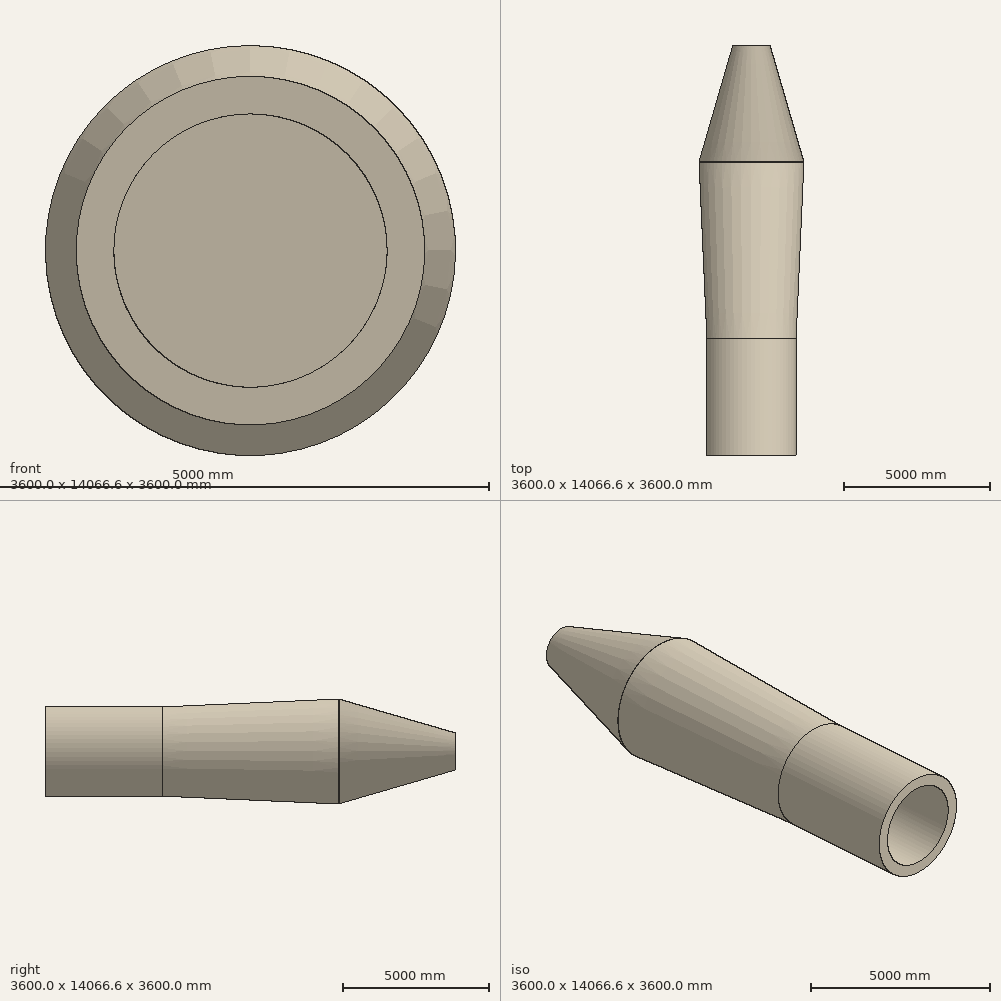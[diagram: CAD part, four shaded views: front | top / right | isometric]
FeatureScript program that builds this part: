
annotation { "Feature Type Name" : "Feature", "Feature Type Description" : "" }
export const myFeature = defineFeature(function(context is Context, id is Id, definition is map)
    precondition{}
    {
        {
            var Q0;
            Q0=qCreatedBy(makeId("Right.planeOp"),FACE);
            var sketch = newSketch(context, id + "F0", { "sketchPlane" : qUnion([Q0])});
            skLineSegment(sketch, "E0", {"start": v(0, 0) * mm, "end": v(-3999.63, 0) * mm});
            skLineSegment(sketch, "E1", {"start": v(-3999.63, 1800) * mm, "end": v(0, 637.5) * mm});
            skLineSegment(sketch, "E2", {"start": v(0, 0) * mm, "end": v(0, 637.5) * mm});
            skLineSegment(sketch, "E3", {"start": v(-3999.63, 0) * mm, "end": v(-10066.63, 0) * mm});
            skLineSegment(sketch, "E4", {"start": v(-10066.63, 1530) * mm, "end": v(-3999.63, 1800) * mm});
            skLineSegment(sketch, "E5", {"start": v(-10066.63, 0) * mm, "end": v(-14066.63, 0) * mm});
            skLineSegment(sketch, "E6", {"start": v(-14066.63, 0) * mm, "end": v(-14066.63, 1530) * mm});
            skLineSegment(sketch, "E7", {"start": v(-14066.63, 1530) * mm, "end": v(-10066.63, 1530) * mm});
            skSolve(sketch);
        }
        {
            var Q0;
            Q0=makeQuery(id+"F0.imprint","IMPRINT",FACE,{"disambiguationData":[TD([[makeQuery(id+"F0.imprint","IMPRINT",EDGE,{"derivedFrom":sQuery(id+"F0.wireOp",EDGE,"E0")}),-1.0]])]});
            var sketch = newSketch(context, id + "F1", { "sketchPlane" : qUnion([Q0])});
            skLineSegment(sketch, "E8", {"start": v(-10067, 0) * mm, "end": v(-2000, 0) * mm});
            skLineSegment(sketch, "E9", {"start": v(-2000, 0) * mm, "end": v(-2000, 1200) * mm});
            skLineSegment(sketch, "E10", {"start": v(-2000, 1200) * mm, "end": v(-10067, 1200) * mm});
            skLineSegment(sketch, "E11", {"start": v(0, 0) * mm, "end": v(0, 1369) * mm, "construction": true});
            skLineSegment(sketch, "E12", {"start": v(0, 1369) * mm, "end": v(-10067, 4000) * mm, "construction": true});
            skLineSegment(sketch, "E13", {"start": v(-10067, 0) * mm, "end": v(0, 0) * mm, "construction": true});
            skLineSegment(sketch, "E14", {"start": v(-10067, 0) * mm, "end": v(-14067.43, 0) * mm});
            skLineSegment(sketch, "E15", {"start": v(-14067.43, 0) * mm, "end": v(-14067.43, 1200) * mm});
            skLineSegment(sketch, "E16", {"start": v(-14067.43, 1200) * mm, "end": v(-10067, 1200) * mm});
            skSolve(sketch);
        }
        {
            var Q0;
            Q0=qCreatedBy(makeId("Right.planeOp"),FACE);
            var sketch = newSketch(context, id + "F2", { "sketchPlane" : qUnion([Q0])});
            skLineSegment(sketch, "E17.bottom", {"start": v(0, 0) * mm, "end": v(-1524, 0) * mm});
            skLineSegment(sketch, "E17.top", {"start": v(0, 630) * mm, "end": v(-1524, 630) * mm});
            skLineSegment(sketch, "E17.left", {"start": v(0, 0) * mm, "end": v(0, 630) * mm});
            skLineSegment(sketch, "E17.right", {"start": v(-1524, 0) * mm, "end": v(-1524, 630) * mm});
            skSolve(sketch);
        }
        {
            var Q0;
            Q0=makeQuery(id+"F0.imprint","IMPRINT",FACE,{"disambiguationData":[TD([[makeQuery(id+"F0.imprint","IMPRINT",EDGE,{"derivedFrom":sQuery(id+"F0.wireOp",EDGE,"E0")}),-1.0]])]});
            var sketch = newSketch(context, id + "F3", { "sketchPlane" : qUnion([Q0])});
            skLineSegment(sketch, "E18", {"start": v(-10067, 0) * mm, "end": v(-10067, 1500) * mm});
            skLineSegment(sketch, "E19", {"start": v(-10067, 1500) * mm, "end": v(-3985, 1798.69) * mm});
            skLineSegment(sketch, "E20", {"start": v(-3985, 1798.69) * mm, "end": v(-3985, 0) * mm});
            skLineSegment(sketch, "E21", {"start": v(-3985, 0) * mm, "end": v(-10067, 0) * mm});
            skSolve(sketch);
        }
        {
            var Q0;
            Q0=qSketchRegion(id+"F0",true);
            var Q1;
            Q1=sQuery(id+"F0.wireOp",EDGE,"E0");
            revolve(context, id + "F4", {"entities" : qUnion([Q0]), "axis" : qUnion([Q1]), "revolveType" : RevolveType.FULL});
        }
        {
            var Q0;
            Q0=qSketchRegion(id+"F1",true);
            var Q1;
            Q1=sQuery(id+"F1.wireOp",EDGE,"E8");
            revolve(context, id + "F5", {"operationType" : NewBodyOperationType.REMOVE, "entities" : qUnion([Q0]), "axis" : qUnion([Q1]), "revolveType" : RevolveType.FULL, "oppositeDirection" : true});
        }
        {
            var Q0;
            Q0 = qSketchRegion(id + "F2", true);
            var Q1;
            Q1=sQuery(id+"F0.wireOp",EDGE,"E0");
            revolve(context, id + "F6", {"operationType" : NewBodyOperationType.REMOVE, "entities" : qUnion([Q0]), "axis" : qUnion([Q1]), "revolveType" : RevolveType.FULL});
        }
        {
            var Q0;
            Q0 = qSketchRegion(id + "F3", true);
            var Q1;
            Q1=sQuery(id+"F0.wireOp",EDGE,"E3");
            revolve(context, id + "F7", {"operationType" : NewBodyOperationType.REMOVE, "entities" : qUnion([Q0]), "axis" : qUnion([Q1]), "revolveType" : RevolveType.FULL, "oppositeDirection" : true});
        }
    });
